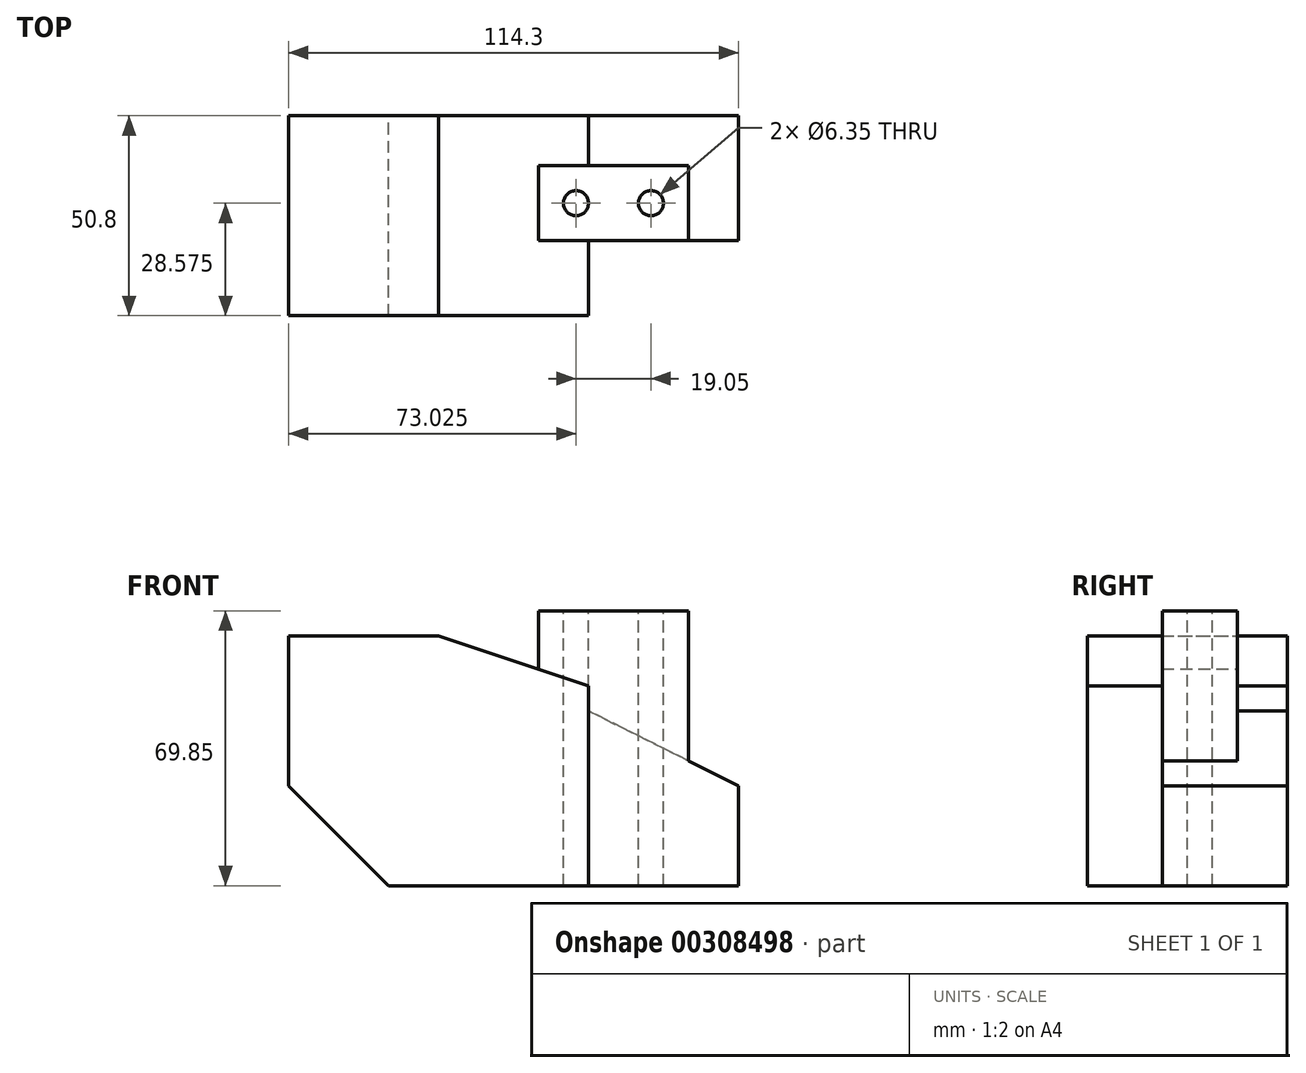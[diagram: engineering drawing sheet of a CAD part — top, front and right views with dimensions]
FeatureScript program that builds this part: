
annotation { "Feature Type Name" : "Feature", "Feature Type Description" : "" }
export const myFeature = defineFeature(function(context is Context, id is Id, definition is map)
    precondition{}
    {
        {
            var Q0;
            Q0=qCreatedBy(makeId("Front.planeOp"),FACE);
            var sketch = newSketch(context, id + "F0", { "sketchPlane" : qUnion([Q0])});
            skLineSegment(sketch, "E0.bottom", {"start": v(0, 0) * mm, "end": v(76.2, 0) * mm, "construction": true});
            skLineSegment(sketch, "E0.top", {"start": v(0, 63.5) * mm, "end": v(76.2, 63.5) * mm, "construction": true});
            skLineSegment(sketch, "E0.left", {"start": v(0, 0) * mm, "end": v(0, 63.5) * mm, "construction": true});
            skLineSegment(sketch, "E0.right", {"start": v(76.2, 0) * mm, "end": v(76.2, 63.5) * mm, "construction": true});
            skLineSegment(sketch, "E1", {"start": v(0, 63.5) * mm, "end": v(0, 25.4) * mm});
            skLineSegment(sketch, "E2", {"start": v(0, 63.5) * mm, "end": v(38.1, 63.5) * mm});
            skLineSegment(sketch, "E3", {"start": v(38.1, 63.5) * mm, "end": v(76.2, 50.8) * mm});
            skLineSegment(sketch, "E4", {"start": v(76.2, 50.8) * mm, "end": v(76.2, 0) * mm});
            skLineSegment(sketch, "E5", {"start": v(25.4, 0) * mm, "end": v(0, 25.4) * mm});
            skLineSegment(sketch, "E6", {"start": v(76.2, 0) * mm, "end": v(25.4, 0) * mm});
            skSolve(sketch);
        }
        {
            var Q0;
            Q0=makeQuery(id+"F0.imprint","IMPRINT",FACE,{"disambiguationData":[TD([[makeQuery(id+"F0.imprint","IMPRINT",EDGE,{"derivedFrom":sQuery(id+"F0.wireOp",EDGE,"E1")}),1.0]])]});
            extrude(context, id + "F1", {"entities" : qUnion([Q0]), "endBound" : BoundingType.SYMMETRIC, "depth" : 50.8 * mm});
        }
        {
            var Q0;
            Q0=makeQuery(id+"F1.opExtrude","SWEPT_FACE",FACE,{"disambiguationData":[OSD([sQuery(id+"F0.wireOp",EDGE,"E4")])]});
            var sketch = newSketch(context, id + "F2", { "sketchPlane" : qUnion([Q0])});
            skLineSegment(sketch, "E7", {"start": v(-6.35, 0) * mm, "end": v(-6.35, 69.85) * mm});
            skLineSegment(sketch, "E8", {"start": v(-6.35, 69.85) * mm, "end": v(12.7, 69.85) * mm});
            skLineSegment(sketch, "E9", {"start": v(12.7, 69.85) * mm, "end": v(12.7, 0) * mm});
            skLineSegment(sketch, "E10", {"start": v(12.7, 0) * mm, "end": v(-6.35, 0) * mm});
            skSolve(sketch);
        }
        {
            var Q0;
            {var subQ0=sQuery(id+"F2.wireOp",EDGE,"E8");Q0=makeQuery(id+"F2.imprint","IMPRINT",FACE,{"disambiguationData":[TD([[makeQuery(id+"F2.imprint","IMPRINT",EDGE,{"derivedFrom":subQ0}),-1.0]])]});}
            var Q1;
            {var subQ0=sQuery(id+"F2.wireOp",EDGE,"E10");Q1=makeQuery(id+"F2.imprint","IMPRINT",FACE,{"disambiguationData":[TD([[makeQuery(id+"F2.imprint","IMPRINT",EDGE,{"derivedFrom":subQ0}),1.0]])]});}
            extrude(context, id + "F3", {"entities" : qUnion([Q0, Q1]), "operationType" : NewBodyOperationType.ADD, "oppositeDirection" : true, "depth" : 12.7 * mm, "hasSecondDirection" : true, "secondDirectionOppositeDirection" : false, "secondDirectionDepth" : 25.4 * mm});
        }
        {
            var Q0;
            Q0=makeQuery(id+"F3.opExtrude","SWEPT_FACE",FACE,{"disambiguationData":[OSD([sQuery(id+"F2.wireOp",EDGE,"E7")])]});
            var sketch = newSketch(context, id + "F4", { "sketchPlane" : qUnion([Q0])});
            skLineSegment(sketch, "E11", {"start": v(114.3, 25.4) * mm, "end": v(114.3, 0) * mm});
            skLineSegment(sketch, "E12", {"start": v(76.2, 0) * mm, "end": v(114.3, 0) * mm});
            skLineSegment(sketch, "E13", {"start": v(76.2, 0) * mm, "end": v(76.2, 44.45) * mm});
            skLineSegment(sketch, "E14", {"start": v(114.3, 25.4) * mm, "end": v(76.2, 44.45) * mm});
            skSolve(sketch);
        }
        {
            var Q0;
            {var subQ4=sQuery(id+"F4.wireOp",EDGE,"E13");Q0=makeQuery(id+"F4.imprint","IMPRINT",FACE,{"disambiguationData":[TD([[makeQuery(id+"F4.imprint","IMPRINT",EDGE,{"derivedFrom":subQ4}),-1.0]])]});}
            var Q1;
            {var subQ0=sQuery(id+"F4.wireOp",EDGE,"E11");Q1=makeQuery(id+"F4.imprint","IMPRINT",FACE,{"disambiguationData":[TD([[makeQuery(id+"F4.imprint","IMPRINT",EDGE,{"derivedFrom":subQ0}),-1.0]])]});}
            var Q2;
            Q2=makeQuery(id+"F1.opExtrude","CAP_FACE",FACE,{"disambiguationData":[OSD([sQuery(id+"F0.wireOp",EDGE,"E1"),sQuery(id+"F0.wireOp",EDGE,"E2"),sQuery(id+"F0.wireOp",EDGE,"E3"),sQuery(id+"F0.wireOp",EDGE,"E4"),sQuery(id+"F0.wireOp",EDGE,"E5"),sQuery(id+"F0.wireOp",EDGE,"E6")])],"isStart":true});
            extrude(context, id + "F5", {"entities" : qUnion([Q0, Q1]), "operationType" : NewBodyOperationType.ADD, "endBound" : BoundingType.UP_TO_SURFACE, "oppositeDirection" : true, "endBoundEntityFace" : qUnion([Q2]), "depth" : 25.4 * mm});
        }
        {
            var Q0;
            Q0=makeQuery(id+"F3.opExtrude","SWEPT_FACE",FACE,{"disambiguationData":[OSD([sQuery(id+"F2.wireOp",EDGE,"E8")])]});
            var sketch = newSketch(context, id + "F6", { "sketchPlane" : qUnion([Q0])});
            skLineSegment(sketch, "E15", {"start": v(63.5, 3.17) * mm, "end": v(101.6, 3.17) * mm, "construction": true});
            skCircle(sketch, "E16", {"center": v(73.03, 3.17) * mm, "radius": 3.18 * mm});
            skCircle(sketch, "E17", {"center": v(92.08, 3.17) * mm, "radius": 3.18 * mm});
            skSolve(sketch);
        }
        {
            var Q0;
            Q0=makeQuery(id+"F6.imprint","IMPRINT",FACE,{"disambiguationData":[TD([[makeQuery(id+"F6.imprint","IMPRINT",EDGE,{"derivedFrom":sQuery(id+"F6.wireOp",EDGE,"E17")}),1.0]])]});
            var Q1;
            Q1=makeQuery(id+"F6.imprint","IMPRINT",FACE,{"disambiguationData":[TD([[makeQuery(id+"F6.imprint","IMPRINT",EDGE,{"derivedFrom":sQuery(id+"F6.wireOp",EDGE,"E16")}),1.0]])]});
            var Q2;
            Q2=makeQuery(id+"F5.boolean.opBoolean","MERGE",FACE,{"derivedFrom":[makeQuery(id+"F3.boolean.opBoolean","MERGE",FACE,{"derivedFrom":[makeQuery(id+"F1.opExtrude","SWEPT_FACE",FACE,{"disambiguationData":[OSD([sQuery(id+"F0.wireOp",EDGE,"E6")])]}),makeQuery(id+"F3.opExtrude","SWEPT_FACE",FACE,{"disambiguationData":[OSD([sQuery(id+"F2.wireOp",EDGE,"E10")])]})]}),makeQuery(id+"F5.opExtrude","SWEPT_FACE",FACE,{"disambiguationData":[OSD([sQuery(id+"F4.wireOp",EDGE,"E12")])]})]});
            extrude(context, id + "F7", {"entities" : qUnion([Q0, Q1]), "operationType" : NewBodyOperationType.REMOVE, "endBound" : BoundingType.UP_TO_SURFACE, "oppositeDirection" : true, "endBoundEntityFace" : qUnion([Q2]), "depth" : 25.4 * mm});
        }
    });
